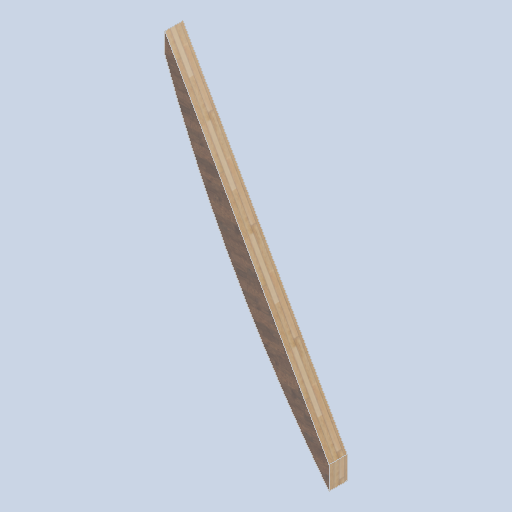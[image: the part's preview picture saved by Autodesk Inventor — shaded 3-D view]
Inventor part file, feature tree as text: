
AUTODESK INVENTOR PART (.ipt)
format: ipt  version: 2024.2 (Build 282272000, 272)  size: 120,832 bytes
history: native  units: in
note: dims shown in document units (in); Inventor stores cm internally (conversion verified against a paired STEP export)
features: other x3, sketch x1
ambient origin geometry x8: Origin, YZ Plane, XZ Plane, XY Plane, X Axis, Y Axis, Z Axis, Center Point
bodies: Body1 (feature_tree)
feature tree (4):
  other  "side_curve_beam_04.ipt"
  other  "Solid2::side_curve_beam_04.ipt"
  other  "TaggingFeature1"
  sketch  "Sketch1"  dims[d0=0.3937in]
